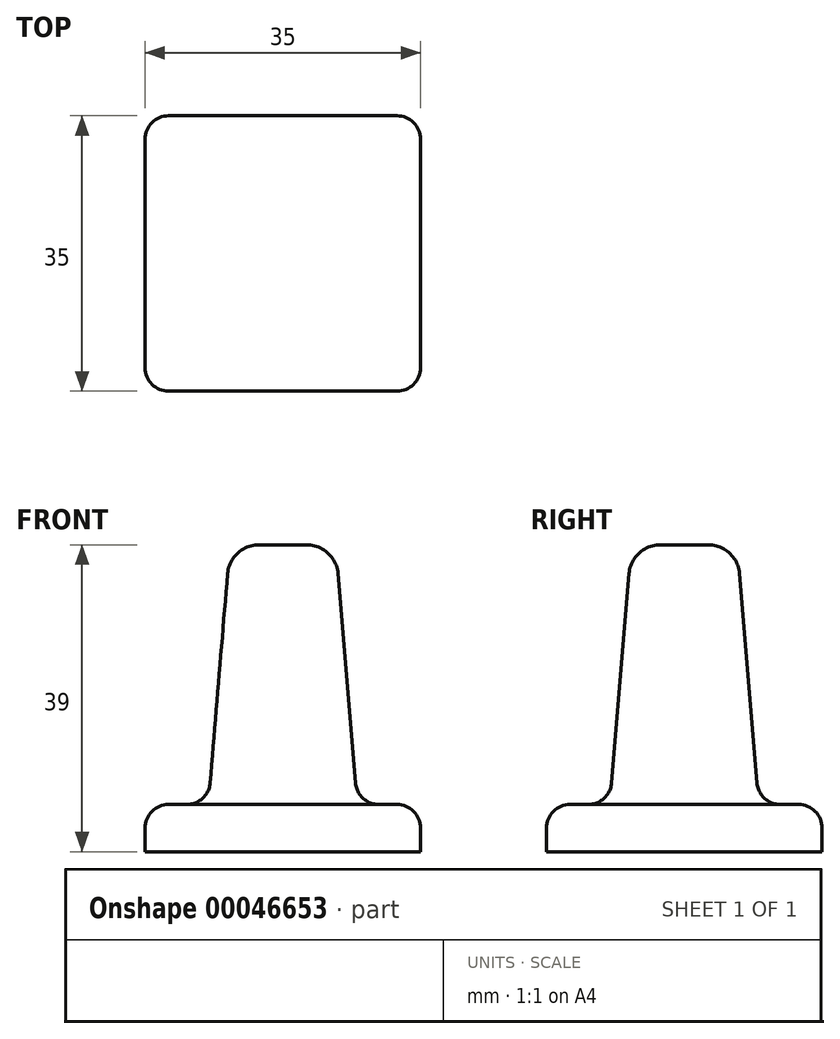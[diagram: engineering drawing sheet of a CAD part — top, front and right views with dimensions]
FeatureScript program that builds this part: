
annotation { "Feature Type Name" : "Feature", "Feature Type Description" : "" }
export const myFeature = defineFeature(function(context is Context, id is Id, definition is map)
    precondition{}
    {
        {
            var Q0;
            Q0=qCreatedBy(makeId("Top.planeOp"),FACE);
            var sketch = newSketch(context, id + "F0", { "sketchPlane" : qUnion([Q0])});
            skLineSegment(sketch, "E0.bottom", {"start": v(-17.5, 17.5) * mm, "end": v(17.5, 17.5) * mm});
            skLineSegment(sketch, "E0.top", {"start": v(-17.5, -17.5) * mm, "end": v(17.5, -17.5) * mm});
            skLineSegment(sketch, "E0.left", {"start": v(-17.5, 17.5) * mm, "end": v(-17.5, -17.5) * mm});
            skLineSegment(sketch, "E0.right", {"start": v(17.5, 17.5) * mm, "end": v(17.5, -17.5) * mm});
            skCircle(sketch, "E1", {"center": v(0, 0) * mm, "radius": 7.96 * mm});
            skSolve(sketch);
        }
        {
            var Q0;
            Q0=makeQuery(id+"F0.imprint","IMPRINT",FACE,{"disambiguationData":[TD([[makeQuery(id+"F0.imprint","IMPRINT",EDGE,{"derivedFrom":sQuery(id+"F0.wireOp",EDGE,"E0.bottom")}),-1.0]])]});
            var Q1;
            Q1=makeQuery(id+"F0.imprint","IMPRINT",FACE,{"disambiguationData":[TD([[makeQuery(id+"F0.imprint","IMPRINT",EDGE,{"derivedFrom":sQuery(id+"F0.wireOp",EDGE,"E1")}),1.0]])]});
            extrude(context, id + "F1", {"entities" : qUnion([Q0, Q1]), "depth" : 6 * mm});
        }
        {
            var Q0;
            Q0=makeQuery(id+"F1.opExtrude","CAP_FACE",FACE,{"disambiguationData":[OSD([sQuery(id+"F0.wireOp",EDGE,"E0.bottom"),sQuery(id+"F0.wireOp",EDGE,"E0.top"),sQuery(id+"F0.wireOp",EDGE,"E0.left"),sQuery(id+"F0.wireOp",EDGE,"E0.right")])],"isStart":false});
            var sketch = newSketch(context, id + "F2", { "sketchPlane" : qUnion([Q0])});
            skCircle(sketch, "E2", {"center": v(0, 0) * mm, "radius": 9.46 * mm});
            skSolve(sketch);
        }
        {
            var Q0;
            Q0=makeQuery(id+"F2.imprint","IMPRINT",FACE,{"disambiguationData":[TD([[makeQuery(id+"F2.imprint","IMPRINT",EDGE,{"derivedFrom":sQuery(id+"F2.wireOp",EDGE,"E2")}),-1.0]])]});
            cPlane(context, id + "F3", {"entities" : qUnion([Q0]), "cplaneType" : CPlaneType.OFFSET, "offset" : 33 * mm, "width" : 150 * mm, "height" : 150 * mm});
        }
        {
            var Q0;
            Q0=qCreatedBy(id+"F3.planeOp",FACE);
            var sketch = newSketch(context, id + "F4", { "sketchPlane" : qUnion([Q0])});
            skCircle(sketch, "E3", {"center": v(0, 0) * mm, "radius": 6.7 * mm});
            skSolve(sketch);
        }
        {
            var Q1;
            Q1=makeQuery(id+"F2.imprint","IMPRINT",FACE,{"disambiguationData":[TD([[makeQuery(id+"F2.imprint","IMPRINT",EDGE,{"derivedFrom":sQuery(id+"F2.wireOp",EDGE,"E2")}),1.0]])]});
            var Q2;
            Q2=makeQuery(id+"F4.imprint","IMPRINT",FACE,{"disambiguationData":[TD([[makeQuery(id+"F4.imprint","IMPRINT",EDGE,{"derivedFrom":sQuery(id+"F4.wireOp",EDGE,"E3")}),1.0]])]});
            loft(context, id + "F5", {"operationType" : NewBodyOperationType.ADD, "sheetProfilesArray" : [{ "sheetProfileEntities" : qUnion([Q1]) }, { "sheetProfileEntities" : qUnion([Q2]) }]});
        }
        {
            var Q0;
            Q0=makeQuery(id+"F5.opLoft","CAP_FACE",FACE,{"disambiguationData":[OSD([makeQuery(id+"F4.imprint","IMPRINT",FACE,{"disambiguationData":[TD([[makeQuery(id+"F4.imprint","IMPRINT",EDGE,{"derivedFrom":sQuery(id+"F4.wireOp",EDGE,"E3")}),1.0]])]})])],"isStart":true});
            fillet(context, id + "F6", {"entities" : qUnion([Q0]), "radius" : 4 * mm, "tangentPropagation" : true, "allowEdgeOverflow" : false});
        }
        {
            var Q0;
            Q0=makeQuery(id+"F1.opExtrude","CAP_FACE",FACE,{"disambiguationData":[OSD([sQuery(id+"F0.wireOp",EDGE,"E0.bottom"),sQuery(id+"F0.wireOp",EDGE,"E0.top"),sQuery(id+"F0.wireOp",EDGE,"E0.left"),sQuery(id+"F0.wireOp",EDGE,"E0.right")])],"isStart":false});
            var Q1;
            Q1=makeQuery(id+"F1.opExtrude","SWEPT_EDGE",EDGE,{"disambiguationData":[OSD([sQuery(id+"F0.wireOp",EDGE,"E0.top"),sQuery(id+"F0.wireOp",EDGE,"E0.left")])]});
            var Q2;
            Q2=makeQuery(id+"F1.opExtrude","SWEPT_EDGE",EDGE,{"disambiguationData":[OSD([sQuery(id+"F0.wireOp",EDGE,"E0.bottom"),sQuery(id+"F0.wireOp",EDGE,"E0.left")])]});
            var Q3;
            Q3=makeQuery(id+"F1.opExtrude","SWEPT_EDGE",EDGE,{"disambiguationData":[OSD([sQuery(id+"F0.wireOp",EDGE,"E0.top"),sQuery(id+"F0.wireOp",EDGE,"E0.right")])]});
            var Q4;
            Q4=makeQuery(id+"F1.opExtrude","SWEPT_EDGE",EDGE,{"disambiguationData":[OSD([sQuery(id+"F0.wireOp",EDGE,"E0.bottom"),sQuery(id+"F0.wireOp",EDGE,"E0.right")])]});
            fillet(context, id + "F7", {"entities" : qUnion([Q0, Q1, Q2, Q3, Q4]), "radius" : 3 * mm, "tangentPropagation" : true, "allowEdgeOverflow" : false});
        }
    });
